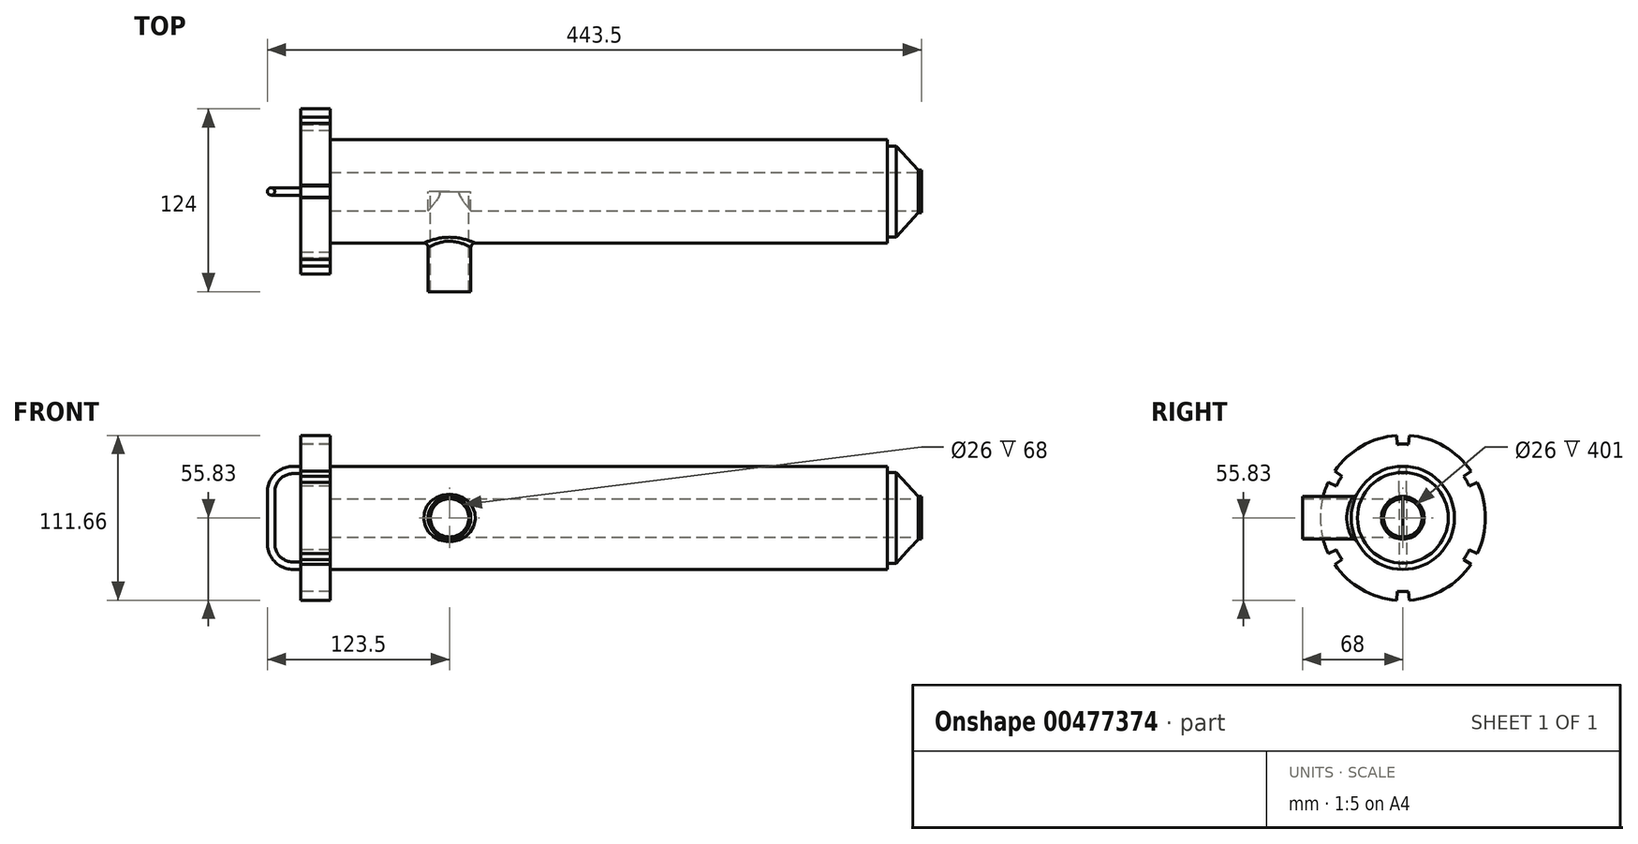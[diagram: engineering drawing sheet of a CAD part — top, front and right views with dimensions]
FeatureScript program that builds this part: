
annotation { "Feature Type Name" : "Feature", "Feature Type Description" : "" }
export const myFeature = defineFeature(function(context is Context, id is Id, definition is map)
    precondition{}
    {
        {
            var Q0;
            Q0=qCreatedBy(makeId("Front.planeOp"),FACE);
            var sketch = newSketch(context, id + "F0", { "sketchPlane" : qUnion([Q0])});
            skLineSegment(sketch, "E0", {"start": v(0, 0) * mm, "end": v(-421, 0) * mm, "construction": true});
            skLineSegment(sketch, "E1", {"start": v(0, 13) * mm, "end": v(-401, 13) * mm});
            skLineSegment(sketch, "E2", {"start": v(-401, 13) * mm, "end": v(-401, 0) * mm});
            skLineSegment(sketch, "E3", {"start": v(-401, 0) * mm, "end": v(-421, 0) * mm});
            skLineSegment(sketch, "E4", {"start": v(-421, 56) * mm, "end": v(-401, 56) * mm});
            skLineSegment(sketch, "E5", {"start": v(-401, 56) * mm, "end": v(-401, 35) * mm});
            skLineSegment(sketch, "E6", {"start": v(-401, 35) * mm, "end": v(-23, 35) * mm});
            skLineSegment(sketch, "E7", {"start": v(-23, 35) * mm, "end": v(-23, 30.8) * mm});
            skLineSegment(sketch, "E8", {"start": v(-23, 30.8) * mm, "end": v(-16.97, 30.8) * mm});
            skLineSegment(sketch, "E9", {"start": v(-16.97, 30.8) * mm, "end": v(-2.26, 14.5) * mm});
            skLineSegment(sketch, "E10", {"start": v(-2.26, 14.5) * mm, "end": v(0, 14.5) * mm});
            skLineSegment(sketch, "E11", {"start": v(0, 14.5) * mm, "end": v(0, 13) * mm});
            skLineSegment(sketch, "E12", {"start": v(-421, 56) * mm, "end": v(-421, 0) * mm});
            skLineSegment(sketch, "E13", {"start": v(-451, 0) * mm, "end": v(-451, 67.51) * mm, "construction": true});
            skSolve(sketch);
        }
        {
            var Q0;
            Q0 = qSketchRegion(id + "F0", true);
            var Q1;
            Q1=sQuery(id+"F0.wireOp",EDGE,"E0");
            revolve(context, id + "F1", {"entities" : qUnion([Q0]), "axis" : qUnion([Q1]), "revolveType" : RevolveType.FULL});
        }
        {
            var Q0;
            Q0=qCreatedBy(makeId("Front.planeOp"),FACE);
            var sketch = newSketch(context, id + "F2", { "sketchPlane" : qUnion([Q0])});
            skLineSegment(sketch, "E14", {"start": v(-441, 0) * mm, "end": v(-441, 17.5) * mm});
            skLineSegment(sketch, "E15.0", {"start": v(-421, 56) * mm, "end": v(-421, -56) * mm});
            skLineSegment(sketch, "E16", {"start": v(-426, 32.5) * mm, "end": v(-421, 32.5) * mm});
            skPoint(sketch, "E17.visualSharp", {"position": v(-441, 32.5) * mm});
            skArc(sketch, "E17.filletArc", {"start": v(-426, 32.5) * mm, "mid": v(-436.6, 28.1) * mm, "end": v(-441, 17.5) * mm});
            skLineSegment(sketch, "E18", {"start": v(-441, 0) * mm, "end": v(-462.2, 0) * mm, "construction": true});
            skLineSegment(sketch, "E19.MirrorCS", {"start": v(-441, 0) * mm, "end": v(-441, -17.5) * mm});
            skPoint(sketch, "E20.MirrorP", {"position": v(-441, -32.5) * mm});
            skArc(sketch, "E21.MirrorCS", {"start": v(-426, -32.5) * mm, "mid": v(-436.6, -28.1) * mm, "end": v(-441, -17.5) * mm});
            skLineSegment(sketch, "E22.MirrorCS", {"start": v(-426, -32.5) * mm, "end": v(-421, -32.5) * mm});
            skSolve(sketch);
        }
        {
            var Q0;
            Q0=makeQuery(id+"F1.opRevolve","SWEPT_FACE",FACE,{"disambiguationData":[OSD([sQuery(id+"F0.wireOp",EDGE,"E12")])]});
            var sketch = newSketch(context, id + "F3", { "sketchPlane" : qUnion([Q0])});
            skPoint(sketch, "E23.0", {"position": v(0, 32.5) * mm});
            skCircle(sketch, "E24", {"center": v(0, 32.5) * mm, "radius": 2.5 * mm});
            skArc(sketch, "E25", {"start": v(3.85, 49.85) * mm, "mid": v(0, 50) * mm, "end": v(-3.85, 49.85) * mm});
            skArc(sketch, "E26.0", {"start": v(4.3, 55.83) * mm, "mid": v(0, 56) * mm, "end": v(-4.3, 55.83) * mm});
            skLineSegment(sketch, "E27.trimOffspring", {"start": v(-3.85, 49.85) * mm, "end": v(-4.3, 55.83) * mm});
            skLineSegment(sketch, "E28.trimOffspring", {"start": v(3.85, 49.85) * mm, "end": v(4.3, 55.83) * mm});
            skArc(sketch, "E29.1.0", {"start": v(50.5, 24.19) * mm, "mid": v(48.5, 28) * mm, "end": v(46.2, 31.65) * mm});
            skLineSegment(sketch, "E29.1.1", {"start": v(45.1, 21.6) * mm, "end": v(50.5, 24.19) * mm});
            skArc(sketch, "E29.1.2", {"start": v(45.1, 21.6) * mm, "mid": v(43.3, 25) * mm, "end": v(41.25, 28.26) * mm});
            skLineSegment(sketch, "E29.1.3", {"start": v(41.25, 28.26) * mm, "end": v(46.2, 31.65) * mm});
            skArc(sketch, "E29.2.0", {"start": v(46.2, -31.65) * mm, "mid": v(48.5, -28) * mm, "end": v(50.5, -24.19) * mm});
            skLineSegment(sketch, "E29.2.1", {"start": v(41.25, -28.26) * mm, "end": v(46.2, -31.65) * mm});
            skArc(sketch, "E29.2.2", {"start": v(41.25, -28.26) * mm, "mid": v(43.3, -25) * mm, "end": v(45.1, -21.6) * mm});
            skLineSegment(sketch, "E29.2.3", {"start": v(45.1, -21.6) * mm, "end": v(50.5, -24.19) * mm});
            skArc(sketch, "E29.3.0", {"start": v(-4.3, -55.83) * mm, "mid": v(0, -56) * mm, "end": v(4.3, -55.83) * mm});
            skLineSegment(sketch, "E29.3.1", {"start": v(-3.85, -49.85) * mm, "end": v(-4.3, -55.83) * mm});
            skArc(sketch, "E29.3.2", {"start": v(-3.85, -49.85) * mm, "mid": v(0, -50) * mm, "end": v(3.85, -49.85) * mm});
            skLineSegment(sketch, "E29.3.3", {"start": v(3.85, -49.85) * mm, "end": v(4.3, -55.83) * mm});
            skArc(sketch, "E29.4.0", {"start": v(-50.5, -24.19) * mm, "mid": v(-48.5, -28) * mm, "end": v(-46.2, -31.65) * mm});
            skLineSegment(sketch, "E29.4.1", {"start": v(-45.1, -21.6) * mm, "end": v(-50.5, -24.19) * mm});
            skArc(sketch, "E29.4.2", {"start": v(-45.1, -21.6) * mm, "mid": v(-43.3, -25) * mm, "end": v(-41.25, -28.26) * mm});
            skLineSegment(sketch, "E29.4.3", {"start": v(-41.25, -28.26) * mm, "end": v(-46.2, -31.65) * mm});
            skArc(sketch, "E29.5.0", {"start": v(-46.2, 31.65) * mm, "mid": v(-48.5, 28) * mm, "end": v(-50.5, 24.19) * mm});
            skLineSegment(sketch, "E29.5.1", {"start": v(-41.25, 28.26) * mm, "end": v(-46.2, 31.65) * mm});
            skArc(sketch, "E29.5.2", {"start": v(-41.25, 28.26) * mm, "mid": v(-43.3, 25) * mm, "end": v(-45.1, 21.6) * mm});
            skLineSegment(sketch, "E29.5.3", {"start": v(-45.1, 21.6) * mm, "end": v(-50.5, 24.19) * mm});
            skLineSegment(sketch, "E29.anchor1", {"start": v(0, 0) * mm, "end": v(-4.3, 55.83) * mm, "construction": true});
            skLineSegment(sketch, "E29.anchor2", {"start": v(0, 0) * mm, "end": v(-50.5, 24.19) * mm, "construction": true});
            skSolve(sketch);
        }
        {
            var Q0;
            Q0=makeQuery(id+"F3.imprint","IMPRINT",FACE,{"disambiguationData":[TD([[makeQuery(id+"F3.imprint","IMPRINT",EDGE,{"derivedFrom":sQuery(id+"F3.wireOp",EDGE,"E24")}),1.0]])]});
            var Q1;
            Q1=sQuery(id+"F2.wireOp",EDGE,"E17.filletArc");
            var Q2;
            Q2=sQuery(id+"F2.wireOp",EDGE,"E14");
            var Q3;
            Q3=sQuery(id+"F2.wireOp",EDGE,"E19.MirrorCS");
            var Q4;
            Q4=sQuery(id+"F2.wireOp",EDGE,"E21.MirrorCS");
            var Q5;
            Q5=sQuery(id+"F2.wireOp",EDGE,"E16");
            var Q6;
            Q6=sQuery(id+"F2.wireOp",EDGE,"E22.MirrorCS");
            sweep(context, id + "F4", {"operationType" : NewBodyOperationType.ADD, "profiles" : qUnion([Q0]), "path" : qUnion([Q1, Q2, Q3, Q4, Q5, Q6])});
        }
        {
            var Q0;
            Q0=makeQuery(id+"F3.imprint","IMPRINT",FACE,{"disambiguationData":[TD([[makeQuery(id+"F3.imprint","IMPRINT",EDGE,{"derivedFrom":sQuery(id+"F3.wireOp",EDGE,"E25")}),-1.0]])]});
            var Q1;
            Q1=makeQuery(id+"F3.imprint","IMPRINT",FACE,{"disambiguationData":[TD([[makeQuery(id+"F3.imprint","IMPRINT",EDGE,{"derivedFrom":sQuery(id+"F3.wireOp",EDGE,"E29.1.0")}),-1.0]])]});
            var Q2;
            Q2=makeQuery(id+"F3.imprint","IMPRINT",FACE,{"disambiguationData":[TD([[makeQuery(id+"F3.imprint","IMPRINT",EDGE,{"derivedFrom":sQuery(id+"F3.wireOp",EDGE,"E29.2.0")}),-1.0]])]});
            var Q3;
            Q3=makeQuery(id+"F3.imprint","IMPRINT",FACE,{"disambiguationData":[TD([[makeQuery(id+"F3.imprint","IMPRINT",EDGE,{"derivedFrom":sQuery(id+"F3.wireOp",EDGE,"E29.3.0")}),-1.0]])]});
            var Q4;
            Q4=makeQuery(id+"F3.imprint","IMPRINT",FACE,{"disambiguationData":[TD([[makeQuery(id+"F3.imprint","IMPRINT",EDGE,{"derivedFrom":sQuery(id+"F3.wireOp",EDGE,"E29.4.0")}),-1.0]])]});
            var Q5;
            Q5=makeQuery(id+"F3.imprint","IMPRINT",FACE,{"disambiguationData":[TD([[makeQuery(id+"F3.imprint","IMPRINT",EDGE,{"derivedFrom":sQuery(id+"F3.wireOp",EDGE,"E29.5.0")}),-1.0]])]});
            extrude(context, id + "F5", {"entities" : qUnion([Q0, Q1, Q2, Q3, Q4, Q5]), "operationType" : NewBodyOperationType.REMOVE, "oppositeDirection" : true, "depth" : 25 * mm});
        }
        {
            var Q0;
            Q0=qCreatedBy(makeId("Front.planeOp"),FACE);
            var sketch = newSketch(context, id + "F6", { "sketchPlane" : qUnion([Q0])});
            skCircle(sketch, "E30", {"center": v(-320, 0) * mm, "radius": 13 * mm});
            skCircle(sketch, "E31", {"center": v(-320, 0) * mm, "radius": 14.5 * mm});
            skSolve(sketch);
        }
        {
            var Q0;
            Q0 = qSketchRegion(id + "F6", true);
            extrude(context, id + "F7", {"entities" : qUnion([Q0]), "operationType" : NewBodyOperationType.ADD, "depth" : 68 * mm});
        }
        {
            var Q0;
            Q0=makeQuery(id+"F7.opExtrude","CAP_FACE",FACE,{"disambiguationData":[OSD([sQuery(id+"F6.wireOp",EDGE,"E30"),sQuery(id+"F6.wireOp",EDGE,"E31")])],"isStart":false});
            var sketch = newSketch(context, id + "F8", { "sketchPlane" : qUnion([Q0])});
            skCircle(sketch, "E32.0", {"center": v(-320, 0) * mm, "radius": 13 * mm});
            skSolve(sketch);
        }
        {
            var Q0;
            Q0 = qSketchRegion(id + "F8", true);
            extrude(context, id + "F9", {"entities" : qUnion([Q0]), "operationType" : NewBodyOperationType.REMOVE, "oppositeDirection" : true, "depth" : 68 * mm});
        }
        {
            var Q0;
            Q0=makeQuery(id+"F7.boolean.opBoolean","INTERSECT",EDGE,{"derivedFrom":[makeQuery(id+"F1.opRevolve","SWEPT_FACE",FACE,{"disambiguationData":[OSD([sQuery(id+"F0.wireOp",EDGE,"E6")])]}),makeQuery(id+"F7.opExtrude","SWEPT_FACE",FACE,{"disambiguationData":[OSD([sQuery(id+"F6.wireOp",EDGE,"E31")])]})]});
            fillet(context, id + "F10", {"entities" : qUnion([Q0]), "radius" : 3 * mm, "tangentPropagation" : true, "allowEdgeOverflow" : false});
        }
    });
